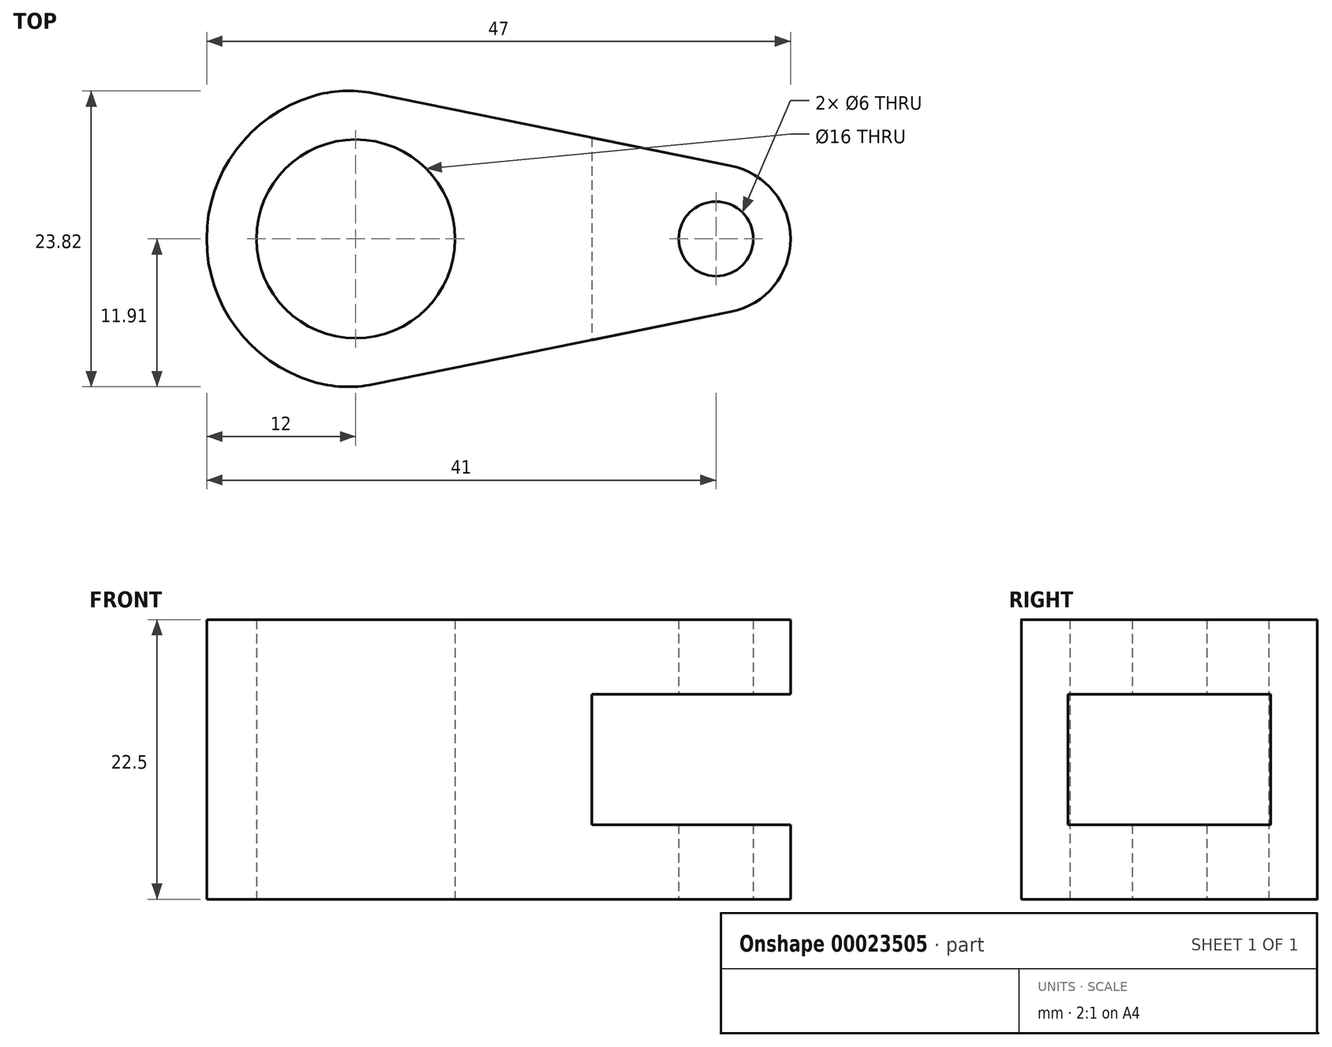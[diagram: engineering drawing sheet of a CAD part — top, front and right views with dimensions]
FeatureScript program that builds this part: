
annotation { "Feature Type Name" : "Feature", "Feature Type Description" : "" }
export const myFeature = defineFeature(function(context is Context, id is Id, definition is map)
    precondition{}
    {
        {
            var Q0;
            Q0=qCreatedBy(makeId("Top.planeOp"),FACE);
            var sketch = newSketch(context, id + "F0", { "sketchPlane" : qUnion([Q0])});
            skArc(sketch, "E0", {"start": v(0, 12) * mm, "mid": v(-12, 0) * mm, "end": v(0, -12) * mm});
            skArc(sketch, "E1", {"start": v(30.2, -5.88) * mm, "mid": v(35, 0) * mm, "end": v(30.2, 5.88) * mm});
            skLineSegment(sketch, "E2", {"start": v(0, 12) * mm, "end": v(30.2, 5.88) * mm});
            skLineSegment(sketch, "E3", {"start": v(0, -12) * mm, "end": v(30.2, -5.88) * mm});
            skCircle(sketch, "E4", {"center": v(0, 0) * mm, "radius": 8 * mm});
            skCircle(sketch, "E5", {"center": v(29, 0) * mm, "radius": 3 * mm});
            skSolve(sketch);
        }
        {
            var Q0;
            Q0 = qSketchRegion(id + "F0", true);
            extrude(context, id + "F1", {"entities" : qUnion([Q0]), "depth" : 22.5 * mm});
        }
        {
            var Q0;
            Q0=makeQuery(id+"F1.opExtrude","SWEPT_EDGE",EDGE,{"disambiguationData":[OSD([sQuery(id+"F0.wireOp",EDGE,"E0"),sQuery(id+"F0.wireOp",EDGE,"E3")])]});
            var Q1;
            Q1=makeQuery(id+"F1.opExtrude","SWEPT_EDGE",EDGE,{"disambiguationData":[OSD([sQuery(id+"F0.wireOp",EDGE,"E0"),sQuery(id+"F0.wireOp",EDGE,"E2")])]});
            fillet(context, id + "F2", {"entities" : qUnion([Q0, Q1]), "radius" : 10 * mm, "tangentPropagation" : true, "allowEdgeOverflow" : false});
        }
        {
            var Q0;
            Q0=qCreatedBy(makeId("Front.planeOp"),FACE);
            var sketch = newSketch(context, id + "F3", { "sketchPlane" : qUnion([Q0])});
            skLineSegment(sketch, "E6", {"start": v(39, 6) * mm, "end": v(19, 6) * mm});
            skLineSegment(sketch, "E7", {"start": v(19, 6) * mm, "end": v(19, 16.5) * mm});
            skLineSegment(sketch, "E8", {"start": v(19, 16.5) * mm, "end": v(39.71, 16.5) * mm});
            skLineSegment(sketch, "E9", {"start": v(39.71, 16.5) * mm, "end": v(39, 6) * mm});
            skSolve(sketch);
        }
        {
            var Q0;
            Q0 = qSketchRegion(id + "F3", true);
            extrude(context, id + "F4", {"entities" : qUnion([Q0]), "operationType" : NewBodyOperationType.REMOVE, "endBound" : BoundingType.SYMMETRIC, "oppositeDirection" : true, "depth" : 25 * mm});
        }
    });
